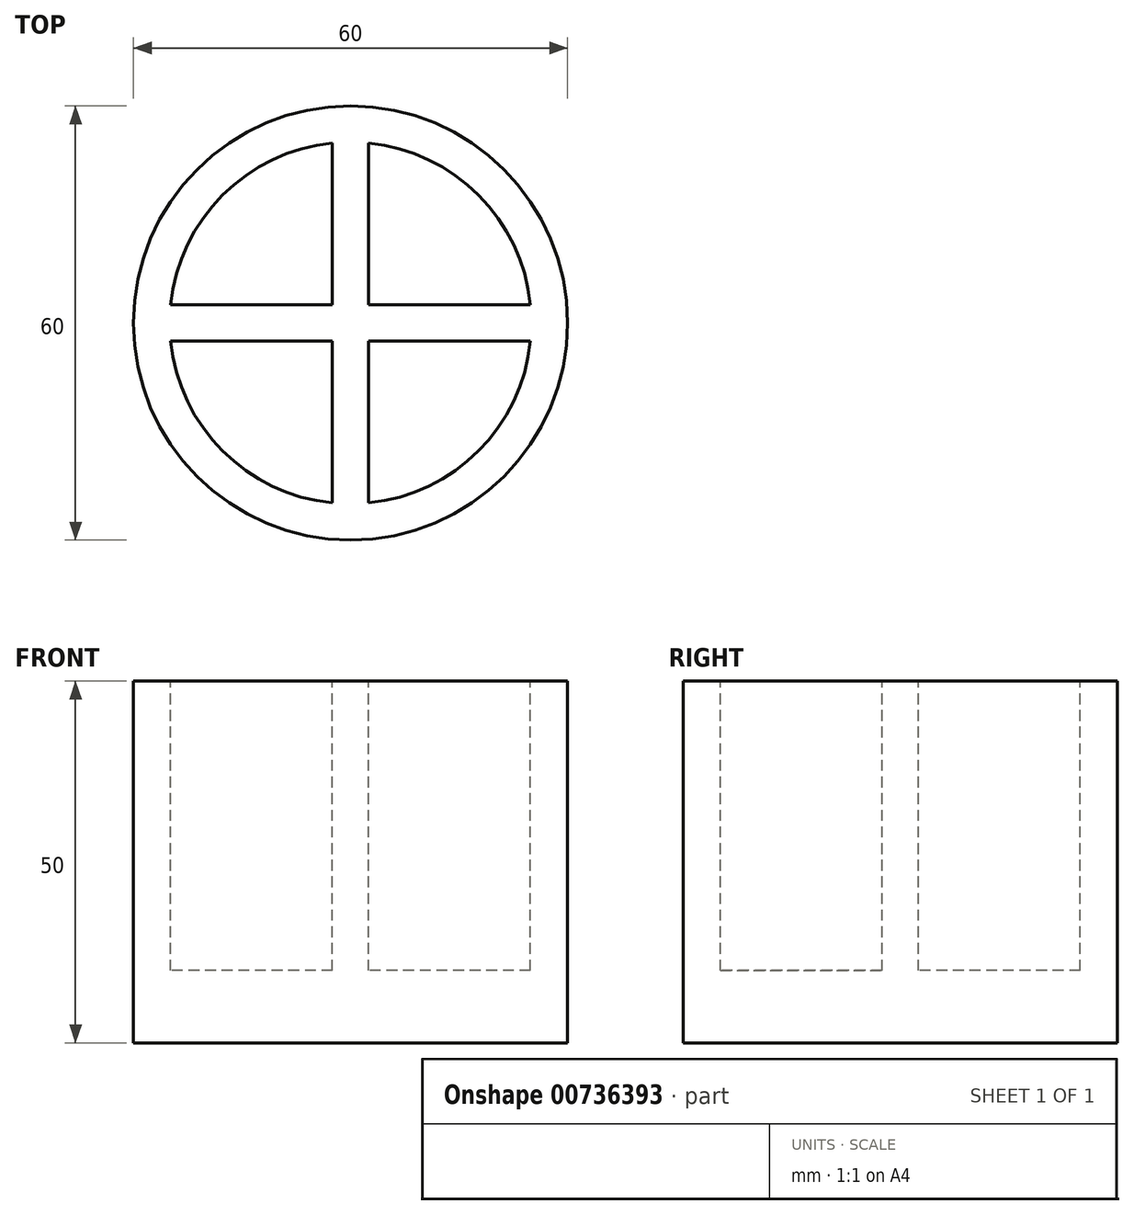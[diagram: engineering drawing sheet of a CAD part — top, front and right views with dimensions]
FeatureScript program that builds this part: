
annotation { "Feature Type Name" : "Feature", "Feature Type Description" : "" }
export const myFeature = defineFeature(function(context is Context, id is Id, definition is map)
    precondition{}
    {
        {
            var Q0;
            Q0=qCreatedBy(makeId("Top.planeOp"),FACE);
            var sketch = newSketch(context, id + "F0", { "sketchPlane" : qUnion([Q0])});
            skCircle(sketch, "E0", {"center": v(0, 0) * mm, "radius": 30 * mm});
            skSolve(sketch);
        }
        {
            var Q0;
            Q0=makeQuery(id+"F0.imprint","IMPRINT",FACE,{"disambiguationData":[TD([[makeQuery(id+"F0.imprint","IMPRINT",EDGE,{"derivedFrom":sQuery(id+"F0.wireOp",EDGE,"E0")}),1.0]])]});
            extrude(context, id + "F1", {"entities" : qUnion([Q0]), "depth" : 50 * mm, "offsetDistance" : 25 * mm});
        }
        {
            var Q0;
            Q0=makeQuery(id+"F1.opExtrude","CAP_FACE",FACE,{"disambiguationData":[OSD([sQuery(id+"F0.wireOp",EDGE,"E0")])],"isStart":false});
            var sketch = newSketch(context, id + "F2", { "sketchPlane" : qUnion([Q0])});
            skCircle(sketch, "E1", {"center": v(0, 0) * mm, "radius": 25 * mm});
            skLineSegment(sketch, "E2.bottom", {"start": v(0, 0) * mm, "end": v(2.5, 0) * mm});
            skLineSegment(sketch, "E2.top", {"start": v(0, 24.87) * mm, "end": v(2.5, 24.87) * mm});
            skLineSegment(sketch, "E2.left", {"start": v(0, 0) * mm, "end": v(0, 24.87) * mm});
            skLineSegment(sketch, "E2.right", {"start": v(2.5, 0) * mm, "end": v(2.5, 24.87) * mm});
            skLineSegment(sketch, "E3.bottom", {"start": v(2.5, 0) * mm, "end": v(0, 0) * mm});
            skLineSegment(sketch, "E3.top", {"start": v(2.5, -25) * mm, "end": v(0, -25) * mm});
            skLineSegment(sketch, "E3.left", {"start": v(2.5, 0) * mm, "end": v(2.5, -25) * mm});
            skLineSegment(sketch, "E3.right", {"start": v(0, 0) * mm, "end": v(0, -25) * mm});
            skLineSegment(sketch, "E4.bottom", {"start": v(0, 24.87) * mm, "end": v(-2.5, 24.87) * mm});
            skLineSegment(sketch, "E4.top", {"start": v(0, -24.87) * mm, "end": v(-2.5, -24.87) * mm});
            skLineSegment(sketch, "E4.left", {"start": v(0, 24.87) * mm, "end": v(0, -24.87) * mm});
            skLineSegment(sketch, "E4.right", {"start": v(-2.5, 24.87) * mm, "end": v(-2.5, -24.87) * mm});
            skLineSegment(sketch, "E5.bottom", {"start": v(0, 0) * mm, "end": v(-24.87, 0) * mm});
            skLineSegment(sketch, "E5.top", {"start": v(0, -2.5) * mm, "end": v(-24.87, -2.5) * mm});
            skLineSegment(sketch, "E5.left", {"start": v(0, 0) * mm, "end": v(0, -2.5) * mm});
            skLineSegment(sketch, "E5.right", {"start": v(-24.87, 0) * mm, "end": v(-24.87, -2.5) * mm});
            skLineSegment(sketch, "E6.bottom", {"start": v(0, -2.5) * mm, "end": v(25, -2.5) * mm});
            skLineSegment(sketch, "E6.top", {"start": v(0, 0) * mm, "end": v(25, 0) * mm});
            skLineSegment(sketch, "E6.left", {"start": v(0, -2.5) * mm, "end": v(0, 0) * mm});
            skLineSegment(sketch, "E6.right", {"start": v(25, -2.5) * mm, "end": v(25, 0) * mm});
            skLineSegment(sketch, "E7.bottom", {"start": v(25, 0) * mm, "end": v(-24.87, 0) * mm});
            skLineSegment(sketch, "E7.top", {"start": v(25, 2.5) * mm, "end": v(-24.87, 2.5) * mm});
            skLineSegment(sketch, "E7.left", {"start": v(25, 0) * mm, "end": v(25, 2.5) * mm});
            skLineSegment(sketch, "E7.right", {"start": v(-24.87, 0) * mm, "end": v(-24.87, 2.5) * mm});
            skSolve(sketch);
        }
        {
            var Q0;
            {var subQ0=sQuery(id+"F2.wireOp",EDGE,"E4.right");var subQ3=sQuery(id+"F2.wireOp",EDGE,"E7.top");var subQ5=makeQuery(id+"F2.imprint","INTERSECT",VERTEX,{"derivedFrom":[subQ0,subQ3]});Q0=makeQuery(id+"F2.imprint","IMPRINT",FACE,{"disambiguationData":[TD([[makeQuery(id+"F2.imprint","IMPRINT",EDGE,{"disambiguationData":[TD([[subQ5,1.0]])],"derivedFrom":subQ0}),-1.0]])]});}
            var Q1;
            {var subQ1=sQuery(id+"F2.wireOp",EDGE,"E1");var subQ3=sQuery(id+"F2.wireOp",EDGE,"E7.top");var subQ4=makeQuery(id+"F2.imprint","INTERSECT",VERTEX,{"derivedFrom":[subQ1,subQ3]});Q1=makeQuery(id+"F2.imprint","IMPRINT",FACE,{"disambiguationData":[TD([[makeQuery(id+"F2.imprint","IMPRINT",EDGE,{"disambiguationData":[TD([[subQ4,-1.0]])],"derivedFrom":subQ3}),-1.0]])]});}
            var Q2;
            {var subQ0=sQuery(id+"F2.wireOp",EDGE,"E3.left");var subQ1=sQuery(id+"F2.wireOp",EDGE,"E1");var subQ2=makeQuery(id+"F2.imprint","INTERSECT",VERTEX,{"derivedFrom":[subQ1,subQ0]});Q2=makeQuery(id+"F2.imprint","IMPRINT",FACE,{"disambiguationData":[TD([[makeQuery(id+"F2.imprint","IMPRINT",EDGE,{"disambiguationData":[TD([[subQ2,-1.0]])],"derivedFrom":subQ1}),1.0]])]});}
            var Q3;
            {var subQ0=sQuery(id+"F2.wireOp",EDGE,"E4.right");var subQ3=sQuery(id+"F2.wireOp",EDGE,"E5.top");var subQ5=makeQuery(id+"F2.imprint","INTERSECT",VERTEX,{"derivedFrom":[subQ0,subQ3]});Q3=makeQuery(id+"F2.imprint","IMPRINT",FACE,{"disambiguationData":[TD([[makeQuery(id+"F2.imprint","IMPRINT",EDGE,{"disambiguationData":[TD([[subQ5,-1.0]])],"derivedFrom":subQ0}),-1.0]])]});}
            extrude(context, id + "F3", {"entities" : qUnion([Q0, Q1, Q2, Q3]), "operationType" : NewBodyOperationType.REMOVE, "oppositeDirection" : true, "depth" : 40 * mm, "offsetDistance" : 25 * mm});
        }
    });
